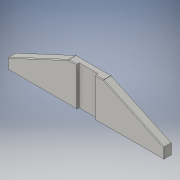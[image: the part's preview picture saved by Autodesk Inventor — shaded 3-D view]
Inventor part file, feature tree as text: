
AUTODESK INVENTOR PART (.ipt)
format: ipt  version: 2016 (Build 200138000, 138)  size: 137,728 bytes
history: native  units: in
note: dims shown in document units (in); Inventor stores cm internally (conversion verified against a paired STEP export)
features: extrude x2, sketch x2, fillet x1
ambient origin geometry x8: Origin, YZ Plane, XZ Plane, XY Plane, X Axis, Y Axis, Z Axis, Center Point
bodies: Solid1 (feature_tree)
feature tree (5):
  extrude  "Extrusion1"  Depth=7.25in
  extrude  "Extrusion2"  Depth=0.125in
  fillet  "Fillet1"  Radius=2.0in
  sketch  "Sketch1"  dims[d0=29.0in d1=7.25in]
  sketch  "Sketch2"  dims[d2=3.25in d3=3.25in d4=2.0in d5=2.0in d6=1.5in d7=0.0in d8=3.5in d9=1.0in d10=7.25in d11=0.0in d12=0.125in]
